# Revit family: QF_Brema_MUSTER1500W
name_source: partatom
category: Specialty Equipment
revit_build: Autodesk Revit MEP 2012 (Build: 20110916_2132(x64)
units: mm (PartAtom-declared; Revit-internal decimal feet)

## types (1)
- MUSTER1500W
    Apparent Power = 6000 VA
    Assembly Code = E1090320
    BTUH = 0 W
    Cold Water Connection Height = 192 mm  [stored 0.629921 ft]
    Cold Water Maximum Pressure = 6.0 bar
    Cold Water Minimum Pressure = 1.0 bar
    Cold Water Size = 1"
    Cold Water Size Radius = 1/2"
    Conn Conduit = Yes
    Cycle = 50 Hz
    Depth = 700 mm  [stored 2.29659 ft]
    Description = AUTOMATIC ICE CUBE MAKER WATER COOLED
    Elec Conn Connection Height = 262 mm  [stored 0.85958 ft]
    FL Amps = 0 A
    Height = 970 mm  [stored 3.18241 ft]
    Indirect Waste Connection Height = 65 mm  [stored 0.213255 ft]
    Indirect Waste Radius = 1/2"
    Indirect Waste Size = 1"
    Manufacturer = BREMA
    Max Overcurrent Protection = 32 A
    Min Ckt Ampacity = 0 A
    Model = MUSTER1500W
    Phase = 3
    Refrigerant Type = R404A
    URL = www.bremaice.it
    Volts = 400 V
    Watts = 6000 W
    Weight = 306 kg
    Width = 1107 mm  [stored 3.63189 ft]

note: [stored X ft] marks values corroborated as IEEE doubles in the binary element streams (Revit-internal decimal feet)

## geometry (parser evidence)
native form markers: Blend x9, Sweep x2
no freeform markers — native parametric forms only
